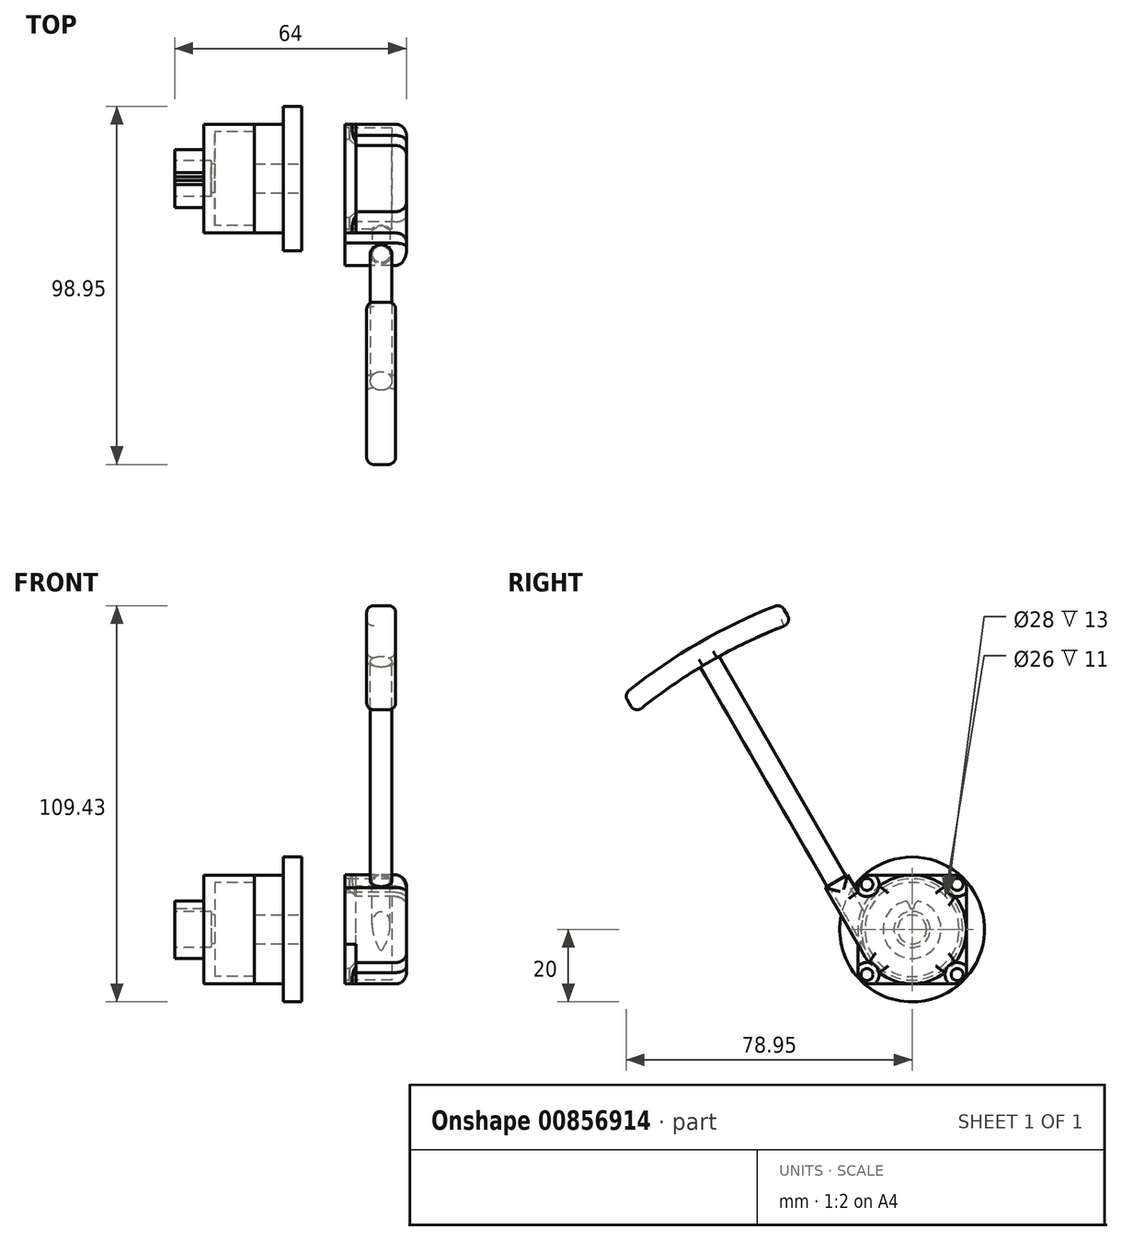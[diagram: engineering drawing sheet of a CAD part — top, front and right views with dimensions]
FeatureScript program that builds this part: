
annotation { "Feature Type Name" : "Feature", "Feature Type Description" : "" }
export const myFeature = defineFeature(function(context is Context, id is Id, definition is map)
    precondition{}
    {
        {
            var Q0;
            Q0=qCreatedBy(makeId("Front.planeOp"),FACE);
            var sketch = newSketch(context, id + "F0", { "sketchPlane" : qUnion([Q0])});
            skLineSegment(sketch, "E0.bottom", {"start": v(0, 15) * mm, "end": v(-14, 15) * mm});
            skLineSegment(sketch, "E0.left", {"start": v(0, 15) * mm, "end": v(0, 0) * mm});
            skLineSegment(sketch, "E0.right", {"start": v(-14, 15) * mm, "end": v(-14, 8) * mm});
            skLineSegment(sketch, "E1", {"start": v(-14, 8) * mm, "end": v(-22, 8) * mm});
            skLineSegment(sketch, "E2", {"start": v(-22, 8) * mm, "end": v(-22, 0) * mm});
            skLineSegment(sketch, "E3", {"start": v(-22, 0) * mm, "end": v(0, 0) * mm});
            skPoint(sketch, "E4.orphan", {"position": v(-22, -8) * mm});
            skLineSegment(sketch, "E5", {"start": v(-35.57, 0) * mm, "end": v(5.94, 0) * mm, "construction": true});
            skSolve(sketch);
        }
        {
            var Q0;
            Q0=makeQuery(id+"F0.imprint","IMPRINT",FACE,{"disambiguationData":[TD([[makeQuery(id+"F0.imprint","IMPRINT",EDGE,{"derivedFrom":sQuery(id+"F0.wireOp",EDGE,"E0.bottom")}),1.0]])]});
            var Q1;
            Q1=sQuery(id+"F0.wireOp",EDGE,"E5");
            revolve(context, id + "F1", {"surfaceOperationType" : NewSurfaceOperationType.NEW, "entities" : qUnion([Q0]), "axis" : qUnion([Q1]), "revolveType" : RevolveType.FULL});
        }
        {
            var Q0;
            Q0=makeQuery(id+"F1.opRevolve","SWEPT_FACE",FACE,{"disambiguationData":[OSD([sQuery(id+"F0.wireOp",EDGE,"E2")])]});
            var sketch = newSketch(context, id + "F2", { "sketchPlane" : qUnion([Q0])});
            skLineSegment(sketch, "E6", {"start": v(0, 0) * mm, "end": v(0, 9.53) * mm, "construction": true});
            skArc(sketch, "E7", {"start": v(0.5, 5.73) * mm, "mid": v(0, 5.75) * mm, "end": v(-0.5, 5.73) * mm});
            skFitSpline(sketch, "E8", {"points": [v(-0.5, 5.73) * mm, v(-1.6, 7.84) * mm], "startDerivative": vector(0, 1.56) * mm, "endDerivative": vector(-2.08, 1.3) * mm});
            skArc(sketch, "E9.0", {"start": v(1.6, 7.84) * mm, "mid": v(0, 8) * mm, "end": v(-1.6, 7.84) * mm});
            skFitSpline(sketch, "E10.MirrorCS", {"points": [v(0.5, 5.73) * mm, v(1.6, 7.84) * mm], "startDerivative": vector(0, 1.56) * mm, "endDerivative": vector(2.08, 1.3) * mm});
            skLineSegment(sketch, "E11", {"start": v(-0.5, 5.73) * mm, "end": v(-0.5, 4.57) * mm, "construction": true});
            skSolve(sketch);
        }
        {
            var Q0;
            Q0 = qSketchRegion(id + "F2", true);
            var Q1;
            Q1=makeQuery(id+"F1.opRevolve","SWEPT_FACE",FACE,{"disambiguationData":[OSD([sQuery(id+"F0.wireOp",EDGE,"E0.right")])]});
            extrude(context, id + "F3", {"entities" : qUnion([Q0]), "operationType" : NewBodyOperationType.REMOVE, "endBound" : BoundingType.UP_TO_SURFACE, "oppositeDirection" : true, "depth" : 25 * mm, "endBoundEntityFace" : qUnion([Q1]), "offsetDistance" : 25 * mm});
        }
        {
            var Q0;
            Q0=qCreatedBy(makeId("Front.planeOp"),FACE);
            var sketch = newSketch(context, id + "F4", { "sketchPlane" : qUnion([Q0])});
            skLineSegment(sketch, "E12.bottom", {"start": v(0, 0) * mm, "end": v(-22, 0) * mm});
            skLineSegment(sketch, "E12.top", {"start": v(0, 13) * mm, "end": v(-11, 13) * mm});
            skLineSegment(sketch, "E12.left", {"start": v(0, 0) * mm, "end": v(0, 13) * mm});
            skLineSegment(sketch, "E12.right", {"start": v(-11, 0) * mm, "end": v(-11, 13) * mm});
            skLineSegment(sketch, "E13", {"start": v(-14, 15) * mm, "end": v(0, 15) * mm, "construction": true});
            skLineSegment(sketch, "E14.0", {"start": v(-14, -15) * mm, "end": v(-14, 15) * mm, "construction": true});
            skLineSegment(sketch, "E15", {"start": v(-12, 5) * mm, "end": v(-22, 5) * mm});
            skLineSegment(sketch, "E16", {"start": v(-22, 5) * mm, "end": v(-22, 0) * mm});
            skLineSegment(sketch, "E17", {"start": v(-11, 4) * mm, "end": v(-12, 4) * mm});
            skLineSegment(sketch, "E18", {"start": v(-12, 4) * mm, "end": v(-12, 5) * mm});
            skLineSegment(sketch, "E19", {"start": v(0, 0) * mm, "end": v(3.87, 0) * mm, "construction": true});
            skSolve(sketch);
        }
        {
            var Q0;
            Q0 = qSketchRegion(id + "F4", true);
            var Q1;
            Q1=sQuery(id+"F4.wireOp",EDGE,"E19");
            revolve(context, id + "F5", {"operationType" : NewBodyOperationType.REMOVE, "surfaceOperationType" : NewSurfaceOperationType.NEW, "entities" : qUnion([Q0]), "axis" : qUnion([Q1]), "revolveType" : RevolveType.FULL});
        }
        {
            var Q0;
            Q0=makeQuery(id+"F1.opRevolve","SWEPT_FACE",FACE,{"disambiguationData":[OSD([sQuery(id+"F0.wireOp",EDGE,"E0.left")])]});
            var sketch = newSketch(context, id + "F6", { "sketchPlane" : qUnion([Q0])});
            skCircle(sketch, "E20.0", {"center": v(0, 0) * mm, "radius": 15 * mm});
            skSolve(sketch);
        }
        {
            var Q0;
            Q0 = qSketchRegion(id + "F6", true);
            extrude(context, id + "F7", {"entities" : qUnion([Q0]), "depth" : 8 * mm, "offsetDistance" : 25 * mm});
        }
        {
            var Q0;
            Q0=makeQuery(id+"F7.opExtrude","CAP_FACE",FACE,{"disambiguationData":[OSD([sQuery(id+"F6.wireOp",EDGE,"E20.0")])],"isStart":false});
            var sketch = newSketch(context, id + "F8", { "sketchPlane" : qUnion([Q0])});
            skCircle(sketch, "E21", {"center": v(0, 0) * mm, "radius": 20 * mm});
            skSolve(sketch);
        }
        {
            var Q0;
            Q0 = qSketchRegion(id + "F8", true);
            extrude(context, id + "F9", {"entities" : qUnion([Q0]), "operationType" : NewBodyOperationType.ADD, "depth" : 5 * mm, "offsetDistance" : 25 * mm});
        }
        {
            var Q0;
            Q0=makeQuery(id+"F9.opExtrude","CAP_FACE",FACE,{"disambiguationData":[OSD([sQuery(id+"F8.wireOp",EDGE,"E21")])],"isStart":false});
            var sketch = newSketch(context, id + "F10", { "sketchPlane" : qUnion([Q0])});
            skCircle(sketch, "E22", {"center": v(0, 0) * mm, "radius": 4 * mm});
            skSolve(sketch);
        }
        {
            var Q0;
            Q0 = qSketchRegion(id + "F10", true);
            extrude(context, id + "F11", {"entities" : qUnion([Q0]), "operationType" : NewBodyOperationType.REMOVE, "oppositeDirection" : true, "depth" : 25 * mm, "offsetDistance" : 25 * mm});
        }
        {
            var Q0;
            Q0=qCreatedBy(makeId("Right.planeOp"),FACE);
            cPlane(context, id + "F12", {"entities" : qUnion([Q0]), "cplaneType" : CPlaneType.OFFSET, "offset" : 25 * mm, "width" : 150 * mm, "height" : 150 * mm});
        }
        {
            var Q0;
            Q0=qCreatedBy(id+"F12.planeOp",FACE);
            var sketch = newSketch(context, id + "F13", { "sketchPlane" : qUnion([Q0])});
            skLineSegment(sketch, "E23.bottom", {"start": v(15, -15) * mm, "end": v(-15, -15) * mm});
            skLineSegment(sketch, "E23.top", {"start": v(15, 15) * mm, "end": v(-15, 15) * mm});
            skLineSegment(sketch, "E23.left", {"start": v(15, -15) * mm, "end": v(15, 15) * mm});
            skLineSegment(sketch, "E23.right", {"start": v(-15, -15) * mm, "end": v(-15, 15) * mm});
            skPoint(sketch, "E23.middle", {"position": v(0, 0) * mm});
            skLineSegment(sketch, "E24.bottom", {"start": v(12.45, 12.45) * mm, "end": v(-12.45, 12.45) * mm, "construction": true});
            skLineSegment(sketch, "E24.top", {"start": v(12.45, -12.45) * mm, "end": v(-12.45, -12.45) * mm, "construction": true});
            skLineSegment(sketch, "E24.left", {"start": v(12.45, 12.45) * mm, "end": v(12.45, -12.45) * mm, "construction": true});
            skLineSegment(sketch, "E24.right", {"start": v(-12.45, 12.45) * mm, "end": v(-12.45, -12.45) * mm, "construction": true});
            skSolve(sketch);
        }
        {
            var Q0;
            Q0 = qSketchRegion(id + "F13", true);
            extrude(context, id + "F14", {"entities" : qUnion([Q0]), "depth" : 3 * mm, "offsetDistance" : 25 * mm});
        }
        {
            var Q0;
            {var subQ0=sQuery(id+"F13.wireOp",EDGE,"E23.left");var subQ1=sQuery(id+"F13.wireOp",EDGE,"E23.top");var subQ2=makeQuery(id+"F14.opExtrude","CAP_FACE",FACE,{"disambiguationData":[OSD([sQuery(id+"F13.wireOp",EDGE,"E23.bottom"),subQ1,subQ0,sQuery(id+"F13.wireOp",EDGE,"E23.right")])],"isStart":false});Q0=makeQuery(id+"F18.boolean.opBoolean","SPLIT",FACE,{"disambiguationData":[TD([subQ2,makeQuery(id+"F14.opExtrude","SWEPT_FACE",FACE,{"disambiguationData":[OSD([subQ1])]}),makeQuery(id+"F14.opExtrude","SWEPT_FACE",FACE,{"disambiguationData":[OSD([subQ0])]}),makeQuery(id+"F18.opExtrude","SWEPT_FACE",FACE,{"disambiguationData":[OSD([sQuery(id+"F17.wireOp",EDGE,"E29")])]})])],"derivedFrom":subQ2});}
            var sketch = newSketch(context, id + "F15", { "sketchPlane" : qUnion([Q0])});
            skPoint(sketch, "E25.0", {"position": v(-12.45, 12.45) * mm});
            skPoint(sketch, "E26.0", {"position": v(12.45, 12.45) * mm});
            skPoint(sketch, "E27.0", {"position": v(12.45, -12.45) * mm});
            skPoint(sketch, "E28.0", {"position": v(-12.45, -12.45) * mm});
            skSolve(sketch);
        }
        {
            var Q0;
            Q0=sQuery(id+"F15.wireOp",VERTEX,"E26.0");
            var Q1;
            Q1=sQuery(id+"F15.wireOp",VERTEX,"E27.0");
            var Q2;
            Q2=sQuery(id+"F15.wireOp",VERTEX,"E28.0");
            var Q3;
            Q3=sQuery(id+"F15.wireOp",VERTEX,"E25.0");
            var Q4;
            Q4=makeQuery(id+"F14.opExtrude","SWEPT_BODY",BODY,{"disambiguationData":[OSD([sQuery(id+"F13.wireOp",EDGE,"E23.bottom"),sQuery(id+"F13.wireOp",EDGE,"E23.top"),sQuery(id+"F13.wireOp",EDGE,"E23.left"),sQuery(id+"F13.wireOp",EDGE,"E23.right")])]});
            hole(context, id + "F16", {"style" : HoleStyle.C_SINK, "endStyle" : HoleEndStyle.BLIND, "standardTappedOrClearance" : lookupTablePath({ "fit" : "Normal", "standard" : "ISO", "size" : "M3", "type" : "Clearance" }), "standardBlindInLast" : lookupTablePath({ "fit" : "Standard", "standard" : "ISO", "size" : "M3", "type" : "Clearance" }), "holeDiameter" : 3.3 * mm, "cSinkDiameter" : 6.72 * mm, "cSinkAngle" : 90 * degree, "majorDiameter" : 5 * mm, "holeDepth" : 14.1 * mm, "isTappedThrough" : true, "tappedDepth" : 12 * mm, "tapClearance" : 3, "locations" : qUnion([Q0, Q1, Q2, Q3]), "scope" : qUnion([Q4])});
        }
        {
            var Q0;
            Q0=makeQuery(id+"F14.opExtrude","CAP_FACE",FACE,{"disambiguationData":[OSD([sQuery(id+"F13.wireOp",EDGE,"E23.bottom"),sQuery(id+"F13.wireOp",EDGE,"E23.top"),sQuery(id+"F13.wireOp",EDGE,"E23.left"),sQuery(id+"F13.wireOp",EDGE,"E23.right")])],"isStart":false});
            var sketch = newSketch(context, id + "F17", { "sketchPlane" : qUnion([Q0])});
            skArc(sketch, "E29", {"start": v(-13, -7.5) * mm, "mid": v(-12.47, -8.34) * mm, "end": v(-11.9, -9.14) * mm});
            skLineSegment(sketch, "E30", {"start": v(0, 0) * mm, "end": v(-19.04, 32.98) * mm, "construction": true});
            skLineSegment(sketch, "E31", {"start": v(0, 0) * mm, "end": v(0, 29.7) * mm, "construction": true});
            skLineSegment(sketch, "E32", {"start": v(-24, 11.55) * mm, "end": v(-13, -7.5) * mm});
            skArc(sketch, "E33.0", {"start": v(9.14, 11.9) * mm, "mid": v(10.07, 10.07) * mm, "end": v(11.9, 9.14) * mm});
            skArc(sketch, "E34.0", {"start": v(11.9, -9.14) * mm, "mid": v(10.07, -10.07) * mm, "end": v(9.14, -11.9) * mm});
            skArc(sketch, "E35.0", {"start": v(-9.14, -11.9) * mm, "mid": v(-10.07, -10.07) * mm, "end": v(-11.9, -9.14) * mm});
            skArc(sketch, "E36.trimOffspring", {"start": v(-9.14, -11.9) * mm, "mid": v(0, -15) * mm, "end": v(9.14, -11.9) * mm});
            skArc(sketch, "E37.trimOffspring", {"start": v(11.9, -9.14) * mm, "mid": v(15, 0) * mm, "end": v(11.9, 9.14) * mm});
            skArc(sketch, "E38.trimOffspring", {"start": v(9.14, 11.9) * mm, "mid": v(0, 15) * mm, "end": v(-9.14, 11.9) * mm});
            skArc(sketch, "E39.0", {"start": v(-15, 10.26) * mm, "mid": v(-10.07, 10.07) * mm, "end": v(-10.26, 15) * mm});
            skLineSegment(sketch, "E40", {"start": v(-15, 10.26) * mm, "end": v(-17.8, 15.12) * mm});
            skLineSegment(sketch, "E41", {"start": v(-17.8, 15.12) * mm, "end": v(-24, 11.55) * mm});
            skSolve(sketch);
        }
        {
            var Q0;
            Q0 = qSketchRegion(id + "F17", true);
            extrude(context, id + "F18", {"entities" : qUnion([Q0]), "operationType" : NewBodyOperationType.ADD, "depth" : 14 * mm, "offsetDistance" : 25 * mm});
        }
        {
            var Q0;
            Q0=makeQuery(id+"F18.opExtrude","CAP_FACE",FACE,{"disambiguationData":[OSD([sQuery(id+"F17.wireOp",EDGE,"E29"),sQuery(id+"F17.wireOp",EDGE,"E32"),sQuery(id+"F17.wireOp",EDGE,"E33.0"),sQuery(id+"F17.wireOp",EDGE,"E34.0"),sQuery(id+"F17.wireOp",EDGE,"E35.0"),sQuery(id+"F17.wireOp",EDGE,"E36.trimOffspring"),sQuery(id+"F17.wireOp",EDGE,"E37.trimOffspring"),sQuery(id+"F17.wireOp",EDGE,"E38.trimOffspring"),sQuery(id+"F17.wireOp",EDGE,"E39.0"),sQuery(id+"F17.wireOp",EDGE,"E40"),sQuery(id+"F17.wireOp",EDGE,"E41")])],"isStart":true});
            var Q1;
            Q1=makeQuery(id+"F18.opExtrude","CAP_FACE",FACE,{"disambiguationData":[OSD([sQuery(id+"F17.wireOp",EDGE,"E29"),sQuery(id+"F17.wireOp",EDGE,"E32"),sQuery(id+"F17.wireOp",EDGE,"E33.0"),sQuery(id+"F17.wireOp",EDGE,"E34.0"),sQuery(id+"F17.wireOp",EDGE,"E35.0"),sQuery(id+"F17.wireOp",EDGE,"E36.trimOffspring"),sQuery(id+"F17.wireOp",EDGE,"E37.trimOffspring"),sQuery(id+"F17.wireOp",EDGE,"E38.trimOffspring"),sQuery(id+"F17.wireOp",EDGE,"E39.0"),sQuery(id+"F17.wireOp",EDGE,"E40"),sQuery(id+"F17.wireOp",EDGE,"E41")])],"isStart":false});
            cPlane(context, id + "F19", {"entities" : qUnion([Q0, Q1]), "cplaneType" : CPlaneType.MID_PLANE, "offset" : 25 * mm, "width" : 150 * mm, "height" : 150 * mm});
        }
        {
            var Q0;
            Q0=qCreatedBy(id+"F19.planeOp",FACE);
            var sketch = newSketch(context, id + "F20", { "sketchPlane" : qUnion([Q0])});
            skLineSegment(sketch, "E42.0", {"start": v(17.8, 15.12) * mm, "end": v(24, 11.55) * mm, "construction": true});
            skLineSegment(sketch, "E43", {"start": v(20.9, 13.34) * mm, "end": v(17.36, 7.21) * mm, "construction": true});
            skLineSegment(sketch, "E44", {"start": v(20.9, 13.34) * mm, "end": v(23.5, 11.84) * mm});
            skLineSegment(sketch, "E45", {"start": v(23.5, 11.84) * mm, "end": v(58.5, 72.46) * mm});
            skLineSegment(sketch, "E46", {"start": v(58.5, 72.46) * mm, "end": v(55.9, 73.96) * mm});
            skLineSegment(sketch, "E47", {"start": v(55.9, 73.96) * mm, "end": v(20.9, 13.34) * mm});
            skSolve(sketch);
        }
        {
            var Q0;
            Q0 = qSketchRegion(id + "F20", true);
            var Q1;
            Q1=sQuery(id+"F20.wireOp",EDGE,"E43");
            revolve(context, id + "F21", {"surfaceOperationType" : NewSurfaceOperationType.NEW, "entities" : qUnion([Q0]), "axis" : qUnion([Q1]), "revolveType" : RevolveType.FULL});
        }
        {
            var Q0;
            Q0=qCreatedBy(id+"F19.planeOp",FACE);
            var sketch = newSketch(context, id + "F22", { "sketchPlane" : qUnion([Q0])});
            skLineSegment(sketch, "E48.0", {"start": v(53.3, 75.46) * mm, "end": v(58.5, 72.46) * mm, "construction": true});
            skLineSegment(sketch, "E49", {"start": v(55.9, 73.96) * mm, "end": v(46.13, 57.05) * mm, "construction": true});
            skArc(sketch, "E50", {"start": v(76.5, 59.64) * mm, "mid": v(55.9, 73.96) * mm, "end": v(33.2, 84.64) * mm});
            skLineSegment(sketch, "E51", {"start": v(76.5, 59.64) * mm, "end": v(79.54, 64.9) * mm});
            skLineSegment(sketch, "E52", {"start": v(36.24, 89.9) * mm, "end": v(33.2, 84.64) * mm});
            skArc(sketch, "E53.0", {"start": v(79.54, 64.9) * mm, "mid": v(58.9, 79.16) * mm, "end": v(36.24, 89.9) * mm});
            skSolve(sketch);
        }
        {
            var Q0;
            Q0=makeQuery(id+"F22.imprint","IMPRINT",FACE,{"disambiguationData":[TD([[makeQuery(id+"F22.imprint","IMPRINT",EDGE,{"derivedFrom":sQuery(id+"F22.wireOp",EDGE,"E50")}),-1.0]])]});
            var Q1;
            Q1=sQuery(id+"F22.wireOp",EDGE,"E53.0");
            extrude(context, id + "F23", {"entities" : qUnion([Q0]), "operationType" : NewBodyOperationType.ADD, "surfaceEntities" : qUnion([Q1]), "depth" : 8 * mm, "offsetDistance" : 25 * mm, "symmetric" : true});
        }
        {
            var Q0;
            Q0=makeQuery(id+"F23.opExtrude","SWEPT_FACE",FACE,{"disambiguationData":[OSD([sQuery(id+"F22.wireOp",EDGE,"E53.0")])]});
            var Q1;
            Q1=makeQuery(id+"F23.opExtrude","CAP_EDGE",EDGE,{"disambiguationData":[OSD([sQuery(id+"F22.wireOp",EDGE,"E50")])],"isStart":true});
            var Q2;
            Q2=makeQuery(id+"F23.opExtrude","CAP_EDGE",EDGE,{"disambiguationData":[OSD([sQuery(id+"F22.wireOp",EDGE,"E50")])],"isStart":false});
            var Q3;
            Q3=makeQuery(id+"F23.opExtrude","SWEPT_FACE",FACE,{"disambiguationData":[OSD([sQuery(id+"F22.wireOp",EDGE,"E52")])]});
            var Q4;
            Q4=makeQuery(id+"F23.opExtrude","SWEPT_FACE",FACE,{"disambiguationData":[OSD([sQuery(id+"F22.wireOp",EDGE,"E51")])]});
            fillet(context, id + "F24", {"entities" : qUnion([Q0, Q1, Q2, Q3, Q4]), "radius" : 2 * mm, "tangentPropagation" : true, "allowEdgeOverflow" : false});
        }
        {
            var Q0;
            Q0=makeQuery(id+"F18.opExtrude","CAP_FACE",FACE,{"disambiguationData":[OSD([sQuery(id+"F17.wireOp",EDGE,"E29"),sQuery(id+"F17.wireOp",EDGE,"E32"),sQuery(id+"F17.wireOp",EDGE,"E33.0"),sQuery(id+"F17.wireOp",EDGE,"E34.0"),sQuery(id+"F17.wireOp",EDGE,"E35.0"),sQuery(id+"F17.wireOp",EDGE,"E36.trimOffspring"),sQuery(id+"F17.wireOp",EDGE,"E37.trimOffspring"),sQuery(id+"F17.wireOp",EDGE,"E38.trimOffspring"),sQuery(id+"F17.wireOp",EDGE,"E39.0"),sQuery(id+"F17.wireOp",EDGE,"E40"),sQuery(id+"F17.wireOp",EDGE,"E41")])],"isStart":false});
            var Q1;
            Q1=makeQuery(id+"F14.opExtrude","SWEPT_EDGE",EDGE,{"disambiguationData":[OSD([sQuery(id+"F13.wireOp",EDGE,"E23.bottom"),sQuery(id+"F13.wireOp",EDGE,"E23.left")])]});
            var Q2;
            Q2=makeQuery(id+"F14.opExtrude","SWEPT_EDGE",EDGE,{"disambiguationData":[OSD([sQuery(id+"F13.wireOp",EDGE,"E23.bottom"),sQuery(id+"F13.wireOp",EDGE,"E23.right")])]});
            var Q3;
            Q3=makeQuery(id+"F14.opExtrude","SWEPT_EDGE",EDGE,{"disambiguationData":[OSD([sQuery(id+"F13.wireOp",EDGE,"E23.top"),sQuery(id+"F13.wireOp",EDGE,"E23.left")])]});
            var Q4;
            Q4=makeQuery(id+"F14.opExtrude","SWEPT_EDGE",EDGE,{"disambiguationData":[OSD([sQuery(id+"F13.wireOp",EDGE,"E23.top"),sQuery(id+"F13.wireOp",EDGE,"E23.right")])]});
            fillet(context, id + "F25", {"entities" : qUnion([Q0, Q1, Q2, Q3, Q4]), "radius" : 3 * mm, "tangentPropagation" : true, "allowEdgeOverflow" : false});
        }
        {
            var Q0;
            Q0=makeQuery(id+"F18.opExtrude","CAP_FACE",FACE,{"disambiguationData":[OSD([sQuery(id+"F17.wireOp",EDGE,"E29"),sQuery(id+"F17.wireOp",EDGE,"E32"),sQuery(id+"F17.wireOp",EDGE,"E33.0"),sQuery(id+"F17.wireOp",EDGE,"E34.0"),sQuery(id+"F17.wireOp",EDGE,"E35.0"),sQuery(id+"F17.wireOp",EDGE,"E36.trimOffspring"),sQuery(id+"F17.wireOp",EDGE,"E37.trimOffspring"),sQuery(id+"F17.wireOp",EDGE,"E38.trimOffspring"),sQuery(id+"F17.wireOp",EDGE,"E39.0"),sQuery(id+"F17.wireOp",EDGE,"E40"),sQuery(id+"F17.wireOp",EDGE,"E41")])],"isStart":true});
            var Q1;
            Q1=makeQuery(id+"F14.opExtrude","CAP_FACE",FACE,{"disambiguationData":[OSD([sQuery(id+"F13.wireOp",EDGE,"E23.bottom"),sQuery(id+"F13.wireOp",EDGE,"E23.top"),sQuery(id+"F13.wireOp",EDGE,"E23.left"),sQuery(id+"F13.wireOp",EDGE,"E23.right")])],"isStart":true});
            extrude(context, id + "F26", {"entities" : qUnion([Q0]), "operationType" : NewBodyOperationType.ADD, "endBound" : BoundingType.UP_TO_SURFACE, "depth" : 25 * mm, "endBoundEntityFace" : qUnion([Q1]), "offsetDistance" : 25 * mm});
        }
        {
            var Q0;
            {var subQ0=sQuery(id+"F13.wireOp",EDGE,"E23.right");var subQ1=sQuery(id+"F13.wireOp",EDGE,"E23.left");var subQ2=sQuery(id+"F13.wireOp",EDGE,"E23.top");var subQ3=sQuery(id+"F13.wireOp",EDGE,"E23.bottom");Q0=makeQuery(id+"F26.boolean.opBoolean","MERGE",FACE,{"derivedFrom":[makeQuery(id+"F14.opExtrude","CAP_FACE",FACE,{"disambiguationData":[OSD([subQ3,subQ2,subQ1,subQ0])],"isStart":true}),makeQuery(id+"F26.opExtrude","CAP_FACE",FACE,{"disambiguationData":[OSD([subQ3,subQ2,subQ1,subQ0])],"isStart":false})]});}
            var sketch = newSketch(context, id + "F27", { "sketchPlane" : qUnion([Q0])});
            skPoint(sketch, "E54.0", {"position": v(0, 0) * mm});
            skCircle(sketch, "E55", {"center": v(0, 0) * mm, "radius": 14 * mm});
            skSolve(sketch);
        }
        {
            var Q0;
            Q0 = qSketchRegion(id + "F27", true);
            extrude(context, id + "F28", {"entities" : qUnion([Q0]), "operationType" : NewBodyOperationType.REMOVE, "oppositeDirection" : true, "depth" : 13 * mm, "offsetDistance" : 25 * mm});
        }
        {
            var Q0;
            {var subQ0=sQuery(id+"F17.wireOp",EDGE,"E41");Q0=makeQuery(id+"F26.boolean.opBoolean","MERGE",FACE,{"derivedFrom":[makeQuery(id+"F18.opExtrude","SWEPT_FACE",FACE,{"disambiguationData":[OSD([subQ0])]}),makeQuery(id+"F26.opExtrude","SWEPT_FACE",FACE,{"disambiguationData":[OSD([subQ0])]})]});}
            var sketch = newSketch(context, id + "F29", { "sketchPlane" : qUnion([Q0])});
            skCircle(sketch, "E56", {"center": v(35, -11.43) * mm, "radius": 2.5 * mm});
            skLineSegment(sketch, "E57", {"start": v(25, -11.43) * mm, "end": v(35, -11.43) * mm, "construction": true});
            skSolve(sketch);
        }
        {
            var Q0;
            Q0=makeQuery(id+"F29.imprint","IMPRINT",FACE,{"disambiguationData":[TD([[makeQuery(id+"F29.imprint","IMPRINT",EDGE,{"derivedFrom":sQuery(id+"F29.wireOp",EDGE,"E56")}),1.0]])]});
            extrude(context, id + "F30", {"entities" : qUnion([Q0]), "operationType" : NewBodyOperationType.REMOVE, "oppositeDirection" : true, "depth" : 22 * mm, "offsetDistance" : 25 * mm});
        }
    });
